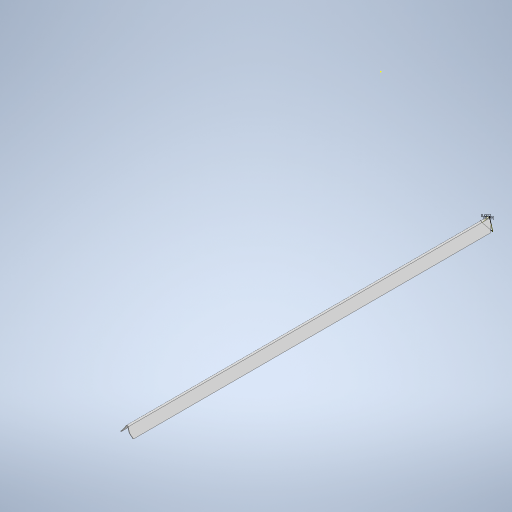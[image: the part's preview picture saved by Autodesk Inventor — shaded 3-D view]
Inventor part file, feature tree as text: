
AUTODESK INVENTOR PART (.ipt)
format: ipt  version: 2023.1 (Build 271208000, 208)  size: 11,617,280 bytes
history: native  units: mm
features: sketch x2, extrude x1
ambient origin geometry x8: Origin, YZ Plane, XZ Plane, XY Plane, X Axis, Y Axis, Z Axis, Center Point
bodies: Solid1 (feature_tree)
feature tree (3):
  extrude  "Extrusion1"  Depth=10.0mm
  sketch  "Sketch2"  dims[d3=9.883022mm]
  sketch  "Sketch1"  dims[d0=10.0mm d1=0.0mm d2=22.0mm]
